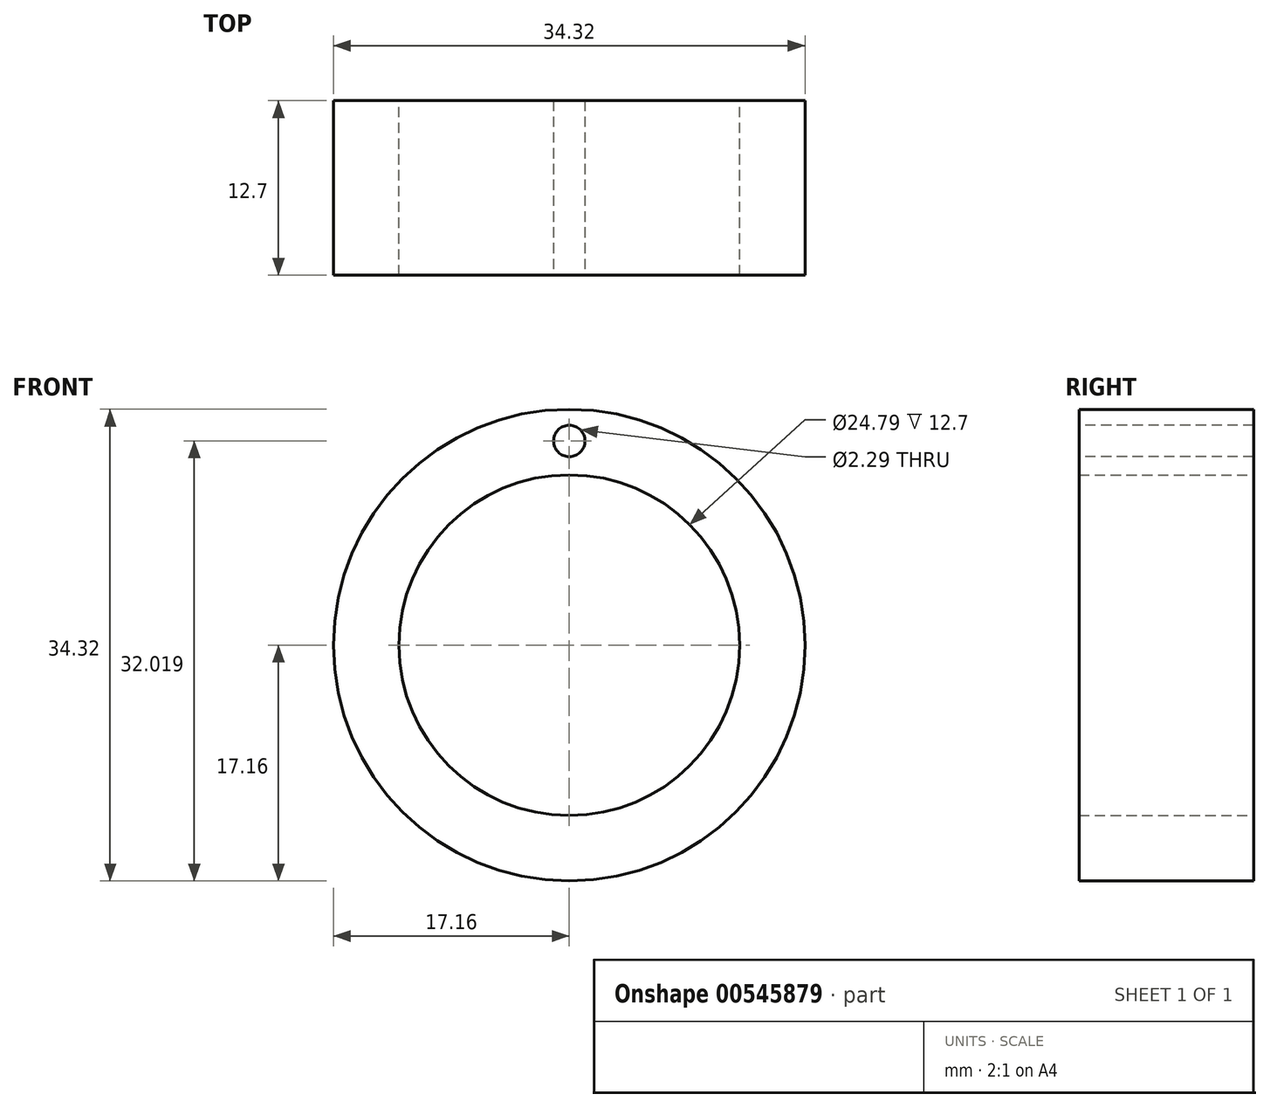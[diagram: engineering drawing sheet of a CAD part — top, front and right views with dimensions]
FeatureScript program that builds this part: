
annotation { "Feature Type Name" : "Feature", "Feature Type Description" : "" }
export const myFeature = defineFeature(function(context is Context, id is Id, definition is map)
    precondition{}
    {
        {
            var Q0;
            Q0=qCreatedBy(makeId("Top.planeOp"),FACE);
            var sketch = newSketch(context, id + "F0", { "sketchPlane" : qUnion([Q0])});
            skLineSegment(sketch, "E0", {"start": v(0, 4.38) * mm, "end": v(0, -7.47) * mm, "construction": true});
            skLineSegment(sketch, "E1", {"start": v(12.4, 6.35) * mm, "end": v(12.4, -6.35) * mm});
            skLineSegment(sketch, "E2", {"start": v(12.4, -6.35) * mm, "end": v(17.16, -6.35) * mm});
            skLineSegment(sketch, "E3", {"start": v(17.16, -6.35) * mm, "end": v(17.16, 6.35) * mm});
            skLineSegment(sketch, "E4", {"start": v(17.16, 6.35) * mm, "end": v(12.4, 6.35) * mm});
            skSolve(sketch);
        }
        {
            var Q0;
            Q0 = qSketchRegion(id + "F0", true);
            var Q1;
            Q1=sQuery(id+"F0.wireOp",EDGE,"E0");
            revolve(context, id + "F1", {"surfaceOperationType" : NewSurfaceOperationType.NEW, "entities" : qUnion([Q0]), "axis" : qUnion([Q1]), "revolveType" : RevolveType.FULL});
        }
        {
            var Q0;
            Q0=qCreatedBy(makeId("Top.planeOp"),FACE);
            var sketch = newSketch(context, id + "F2", { "sketchPlane" : qUnion([Q0])});
            skLineSegment(sketch, "E5.left", {"start": v(1.27, 2.54) * mm, "end": v(1.27, -2.54) * mm});
            skLineSegment(sketch, "E5.right", {"start": v(-1.27, 2.54) * mm, "end": v(-1.27, -2.54) * mm});
            skPoint(sketch, "E5.middle", {"position": v(0, 0) * mm});
            skArc(sketch, "E6", {"start": v(-1.27, 2.54) * mm, "mid": v(0, 3.81) * mm, "end": v(1.27, 2.54) * mm});
            skArc(sketch, "E7", {"start": v(-1.27, -2.54) * mm, "mid": v(0, -3.81) * mm, "end": v(1.27, -2.54) * mm});
            skSolve(sketch);
        }
        {
            var Q0;
            Q0=makeQuery(id+"F1.opRevolve","SWEPT_FACE",FACE,{"disambiguationData":[OSD([sQuery(id+"F0.wireOp",EDGE,"E2")])]});
            var sketch = newSketch(context, id + "F3", { "sketchPlane" : qUnion([Q0])});
            skCircle(sketch, "E8", {"center": v(0, 0) * mm, "radius": 14.86 * mm, "construction": true});
            skCircle(sketch, "E9", {"center": v(0, 14.86) * mm, "radius": 1.14 * mm});
            skSolve(sketch);
        }
        {
            var Q0;
            Q0 = qSketchRegion(id + "F3", true);
            extrude(context, id + "F4", {"entities" : qUnion([Q0]), "operationType" : NewBodyOperationType.REMOVE, "endBound" : BoundingType.UP_TO_NEXT, "oppositeDirection" : true, "depth" : 25.4 * mm, "offsetDistance" : 25.4 * mm});
        }
    });
